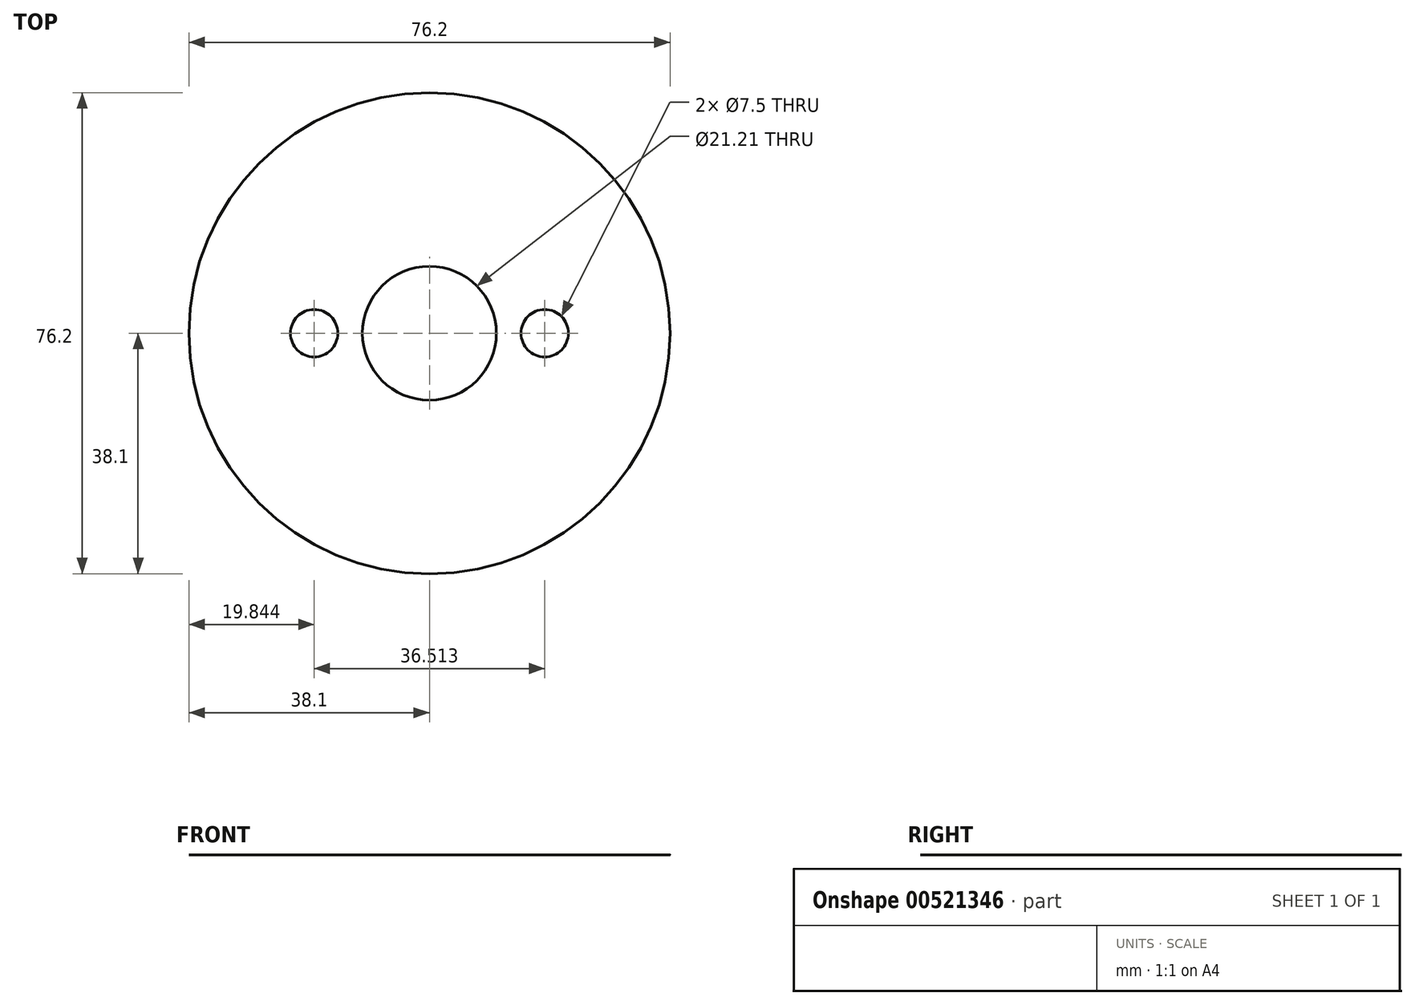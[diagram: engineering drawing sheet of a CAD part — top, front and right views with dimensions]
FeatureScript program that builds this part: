
annotation { "Feature Type Name" : "Feature", "Feature Type Description" : "" }
export const myFeature = defineFeature(function(context is Context, id is Id, definition is map)
    precondition{}
    {
        {
            var Q0;
            Q0=qCreatedBy(makeId("Top.planeOp"),FACE);
            var sketch = newSketch(context, id + "F0", { "sketchPlane" : qUnion([Q0])});
            skCircle(sketch, "E0", {"center": v(0, 0) * mm, "radius": 38.1 * mm});
            skCircle(sketch, "E1", {"center": v(0, 0) * mm, "radius": 10.6 * mm});
            skCircle(sketch, "E2", {"center": v(-18.26, 0) * mm, "radius": 3.75 * mm});
            skLineSegment(sketch, "E3", {"start": v(0, 0) * mm, "end": v(0, 21) * mm, "construction": true});
            skCircle(sketch, "E4.MirrorC", {"center": v(18.26, 0) * mm, "radius": 3.75 * mm});
            skSolve(sketch);
        }
        {
            var Q0;
            Q0 = qSketchRegion(id + "F0", true);
            extrude(context, id + "F1", {"entities" : qUnion([Q0]), "depth" : 1 / 406.4 * mm, "offsetDistance" : 25.4 * mm});
        }
    });
